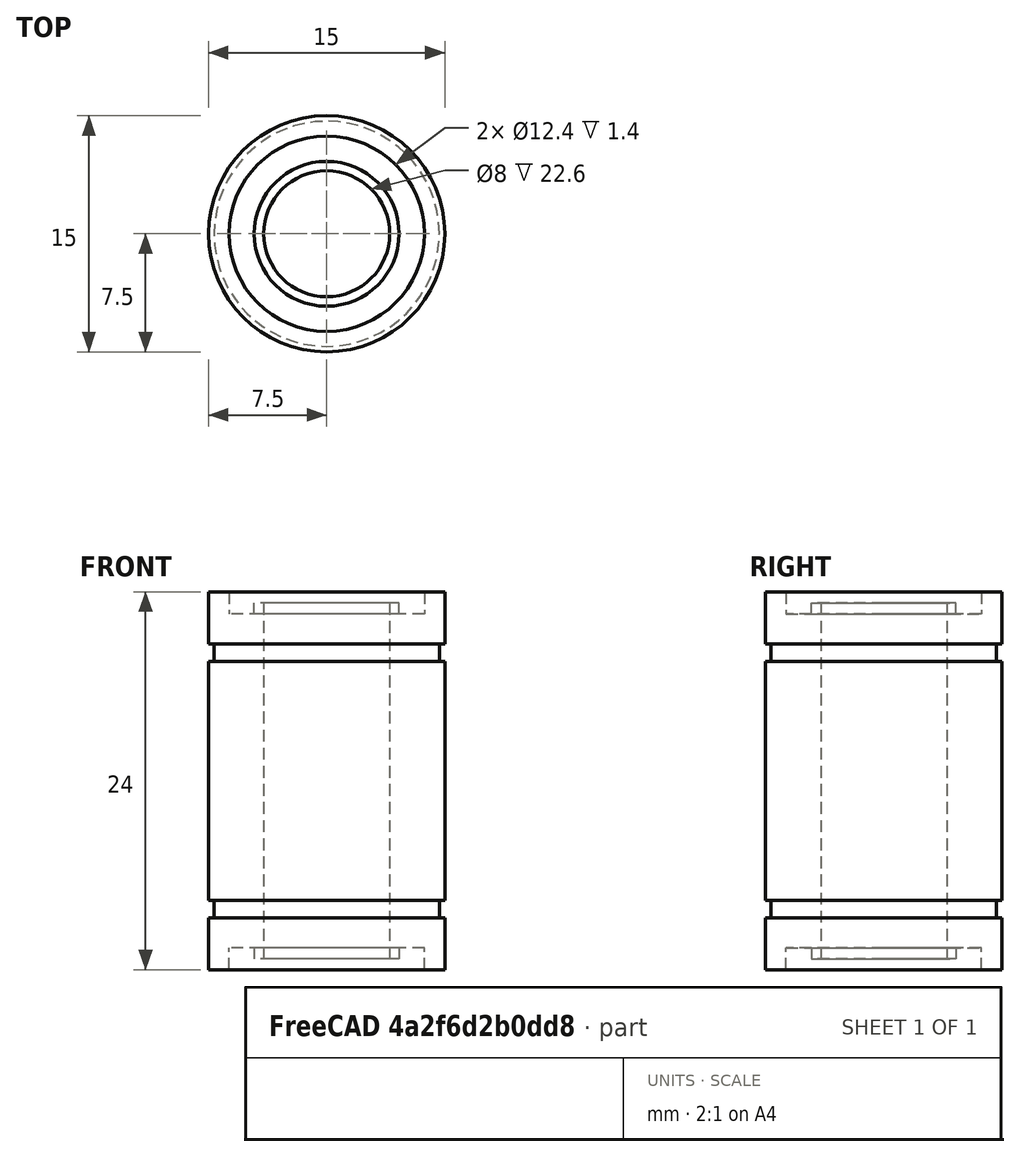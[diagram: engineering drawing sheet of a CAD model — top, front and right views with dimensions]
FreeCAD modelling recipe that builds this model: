
FCSTD DOCUMENT  (FreeCAD 0.18R16110 (Git))
Label: LM8uu
License: CC-BY 3.0
LicenseURL: http://creativecommons.org/licenses/by/3.0/
objects: Sketcher::SketchObject×1, PartDesign::Revolution×1, Part::Feature×1
note: 4 computed .brp shape members not serialized (recipe doc carries the construction recipe); baked Part::Feature solids carry a one-line shape summary decoded from their .brp

FEATURE [Sketcher::SketchObject] Sketch  label="lm8uu-cross-section"
  MapMode = 5
  Placement = pos=(0,0,0) rot=(1,0,0;1.5708rad)
  sketch-geometry (20):
    g0: LineSegment StartX=7.5 StartY=-12 StartZ=0 EndX=7.5 EndY=-8.7 EndZ=0
    g1: LineSegment StartX=7.5 StartY=7.6 StartZ=0 EndX=7.15 EndY=7.6 EndZ=0
    g2: LineSegment StartX=7.15 StartY=7.6 StartZ=0 EndX=7.15 EndY=8.7 EndZ=0
    g3: LineSegment StartX=7.15 StartY=8.7 StartZ=0 EndX=7.5 EndY=8.7 EndZ=0
    g4: LineSegment StartX=7.5 StartY=8.7 StartZ=0 EndX=7.5 EndY=12 EndZ=0
    g5: LineSegment StartX=7.5 StartY=12 StartZ=0 EndX=6.2 EndY=12 EndZ=0
    g6: LineSegment StartX=6.2 StartY=12 StartZ=0 EndX=6.2 EndY=10.6 EndZ=0
    g7: LineSegment StartX=6.2 StartY=10.6 StartZ=0 EndX=4.6 EndY=10.6 EndZ=0
    g8: LineSegment StartX=4.6 StartY=10.6 StartZ=0 EndX=4.6 EndY=11.3 EndZ=0
    g9: LineSegment StartX=4.6 StartY=11.3 StartZ=0 EndX=4 EndY=11.3 EndZ=0
    g10: LineSegment StartX=4 StartY=11.3 StartZ=0 EndX=4 EndY=-11.3 EndZ=0
    g11: LineSegment StartX=7.5 StartY=-7.6 StartZ=0 EndX=7.15 EndY=-7.6 EndZ=0
    g12: LineSegment StartX=7.15 StartY=-8.7 StartZ=0 EndX=7.5 EndY=-8.7 EndZ=0
    g13: LineSegment StartX=7.5 StartY=-7.6 StartZ=0 EndX=7.5 EndY=7.6 EndZ=0
    g14: LineSegment StartX=7.15 StartY=-7.6 StartZ=0 EndX=7.15 EndY=-8.7 EndZ=0
    g15: LineSegment StartX=7.5 StartY=-12 StartZ=0 EndX=6.2 EndY=-12 EndZ=0
    g16: LineSegment StartX=6.2 StartY=-12 StartZ=0 EndX=6.2 EndY=-10.6 EndZ=0
    g17: LineSegment StartX=6.2 StartY=-10.6 StartZ=0 EndX=4.6 EndY=-10.6 EndZ=0
    g18: LineSegment StartX=4.6 StartY=-10.6 StartZ=0 EndX=4.6 EndY=-11.3 EndZ=0
    g19: LineSegment StartX=4.6 StartY=-11.3 StartZ=0 EndX=4 EndY=-11.3 EndZ=0
  constraints (58):
    c: Coincident(g13,g1)
    c: Coincident(g1,g2)
    c: Vertical(g2)
    c: Coincident(g2,g3)
    c: Coincident(g3,g4)
    c: Vertical(g4)
    c: Coincident(g4,g5)
    c: Coincident(g5,g6)
    c: Vertical(g6)
    c: Coincident(g6,g7)
    c: Horizontal(g7)
    c: Coincident(g7,g8)
    c: Vertical(g8)
    c: Coincident(g8,g9)
    c: Horizontal(g9)
    c: Coincident(g9,g10)
    c: Vertical(g10)
    c: Horizontal(g1)
    c: Horizontal(g5)
    c: Horizontal(g3)
    c: PointOnObject(g3,g0)
    c: Symmetric(g0,g4,g-1)
    c: DistanceY(g4,g0) = -24
    c: DistanceY(g2) = 1.1
    c: DistanceX(g3) = 0.35
    c: DistanceX(g-1,g4) = 7.5
    c: DistanceX(g-1,g9) = 4
    c: DistanceX(g5) = -1.3
    c: DistanceX(g9) = -0.6
    c: DistanceY(g6) = -1.4
    c: DistanceY(g8) = 0.7
    c: Horizontal(g11)
    c: Horizontal(g12)
    c: Coincident(g13,g11)
    c: Tangent(g0,g13)
    c: Coincident(g12,g0)
    c: PointOnObject(g14,g11)
    c: Coincident(g14,g12)
    c: Vertical(g14)
    c: Symmetric(g1,g11,g-1)
    c: DistanceY(g13) = 15.2
    c: Equal(g14,g2)
    c: Coincident(g0,g15)
    c: Horizontal(g15)
    c: Coincident(g15,g16)
    c: Vertical(g16)
    c: Coincident(g16,g17)
    c: Horizontal(g17)
    c: Coincident(g17,g18)
    c: Vertical(g18)
    c: Coincident(g18,g19)
    c: Horizontal(g19)
    c: Coincident(g10,g19)
    c: Symmetric(g10,g9,g-1)
    c: Symmetric(g16,g6,g-1)
    c: Symmetric(g17,g7,g-1)
    c: Coincident(g14,g11)
    c: PointOnObject(g11,g2)
FEATURE [PartDesign::Revolution] Revolution  label="LM8uu"
  Angle = 360
  Axis = (0,0,1)
  Base = (0,0,0)
  Placement = pos=(0,0,0) rot=(1,0,0;1.5708rad)
  Profile = -> Sketch
  ReferenceAxis = -> Sketch [V_Axis]
  Reversed = true
FEATURE [Part::Feature] Revolution001  label="LM8uu001"
  Placement = pos=(0,0,0) rot=(1,0,0;1.5708rad)
  shape: bbox 15 x 15 x 24 mm, 20 faces (baked)
